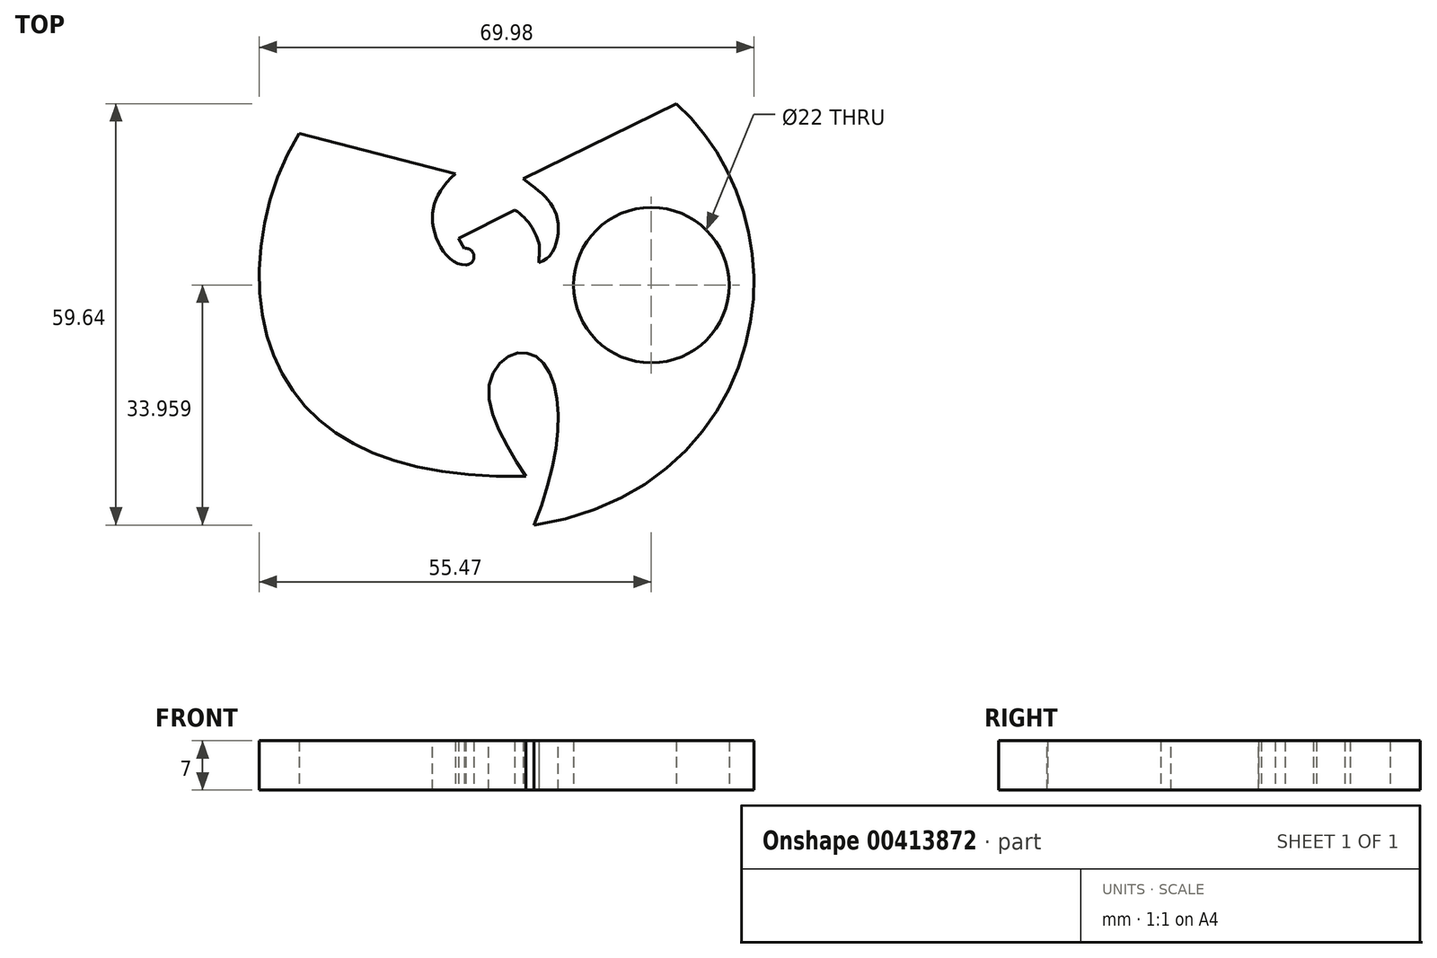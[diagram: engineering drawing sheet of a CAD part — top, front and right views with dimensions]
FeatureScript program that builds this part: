
annotation { "Feature Type Name" : "Feature", "Feature Type Description" : "" }
export const myFeature = defineFeature(function(context is Context, id is Id, definition is map)
    precondition{}
    {
        {
            var Q0;
            Q0=qCreatedBy(makeId("Top.planeOp"),FACE);
            var sketch = newSketch(context, id + "F0", { "sketchPlane" : qUnion([Q0])});
            skArc(sketch, "E0", {"start": v(-5.72, 6.83) * mm, "mid": v(-4.56, 8.1) * mm, "end": v(-5.94, 9.14) * mm});
            skLineSegment(sketch, "E1", {"start": v(-5.94, 9.14) * mm, "end": v(-6.76, 10.56) * mm});
            skLineSegment(sketch, "E2", {"start": v(-6.76, 10.56) * mm, "end": v(1.2, 14.57) * mm});
            skFitSpline(sketch, "E3", {"points": [v(1.2, 14.57) * mm, v(4.53, 10.2) * mm, v(4.61, 7.15) * mm], "startDerivative": vector(8.3, -4.32) * mm, "endDerivative": vector(-0.33, -8.29) * mm});
            skFitSpline(sketch, "E4", {"points": [v(4.61, 7.15) * mm, v(7.2, 13.54) * mm, v(2.42, 19) * mm], "startDerivative": vector(14.39, 3.3) * mm, "endDerivative": vector(-13.13, 10.23) * mm});
            skLineSegment(sketch, "E5", {"start": v(2.42, 19) * mm, "end": v(24.06, 29.64) * mm});
            skFitSpline(sketch, "E6", {"points": [v(24.06, 29.64) * mm, v(34.76, 0) * mm, v(3.95, -30) * mm], "startDerivative": vector(49.8, -45.42) * mm, "endDerivative": vector(-106.2, -15.94) * mm});
            skFitSpline(sketch, "E7", {"points": [v(3.95, -30) * mm, v(7.32, -13.65) * mm, v(4.73, -6.53) * mm, v(0.85, -5.89) * mm, v(-2.48, -10.97) * mm, v(2.79, -23.07) * mm], "startDerivative": vector(25.96, 64.8) * mm, "endDerivative": vector(29.7, -44.79) * mm});
            skFitSpline(sketch, "E8", {"points": [v(2.79, -23.07) * mm, v(-24.84, -16.42) * mm, v(-34.54, 0) * mm, v(-29.26, 25.4) * mm], "startDerivative": vector(-98.98, -2.11) * mm, "endDerivative": vector(41.71, 66.36) * mm});
            skLineSegment(sketch, "E9", {"start": v(-29.26, 25.4) * mm, "end": v(-7.16, 19.73) * mm});
            skFitSpline(sketch, "E10", {"points": [v(-7.16, 19.73) * mm, v(-10.3, 12.15) * mm, v(-5.72, 6.83) * mm], "startDerivative": vector(-15.48, -13.88) * mm, "endDerivative": vector(14.2, 0.78) * mm});
            skCircle(sketch, "E11", {"center": v(20.53, 3.96) * mm, "radius": 11 * mm});
            skSolve(sketch);
        }
        {
            var Q0;
            Q0=makeQuery(id+"F0.imprint","IMPRINT",FACE,{"disambiguationData":[TD([[makeQuery(id+"F0.imprint","IMPRINT",EDGE,{"derivedFrom":sQuery(id+"F0.wireOp",EDGE,"E0")}),-1.0]])]});
            extrude(context, id + "F1", {"entities" : qUnion([Q0]), "endBound" : BoundingType.SYMMETRIC, "depth" : 7 * mm});
        }
    });
